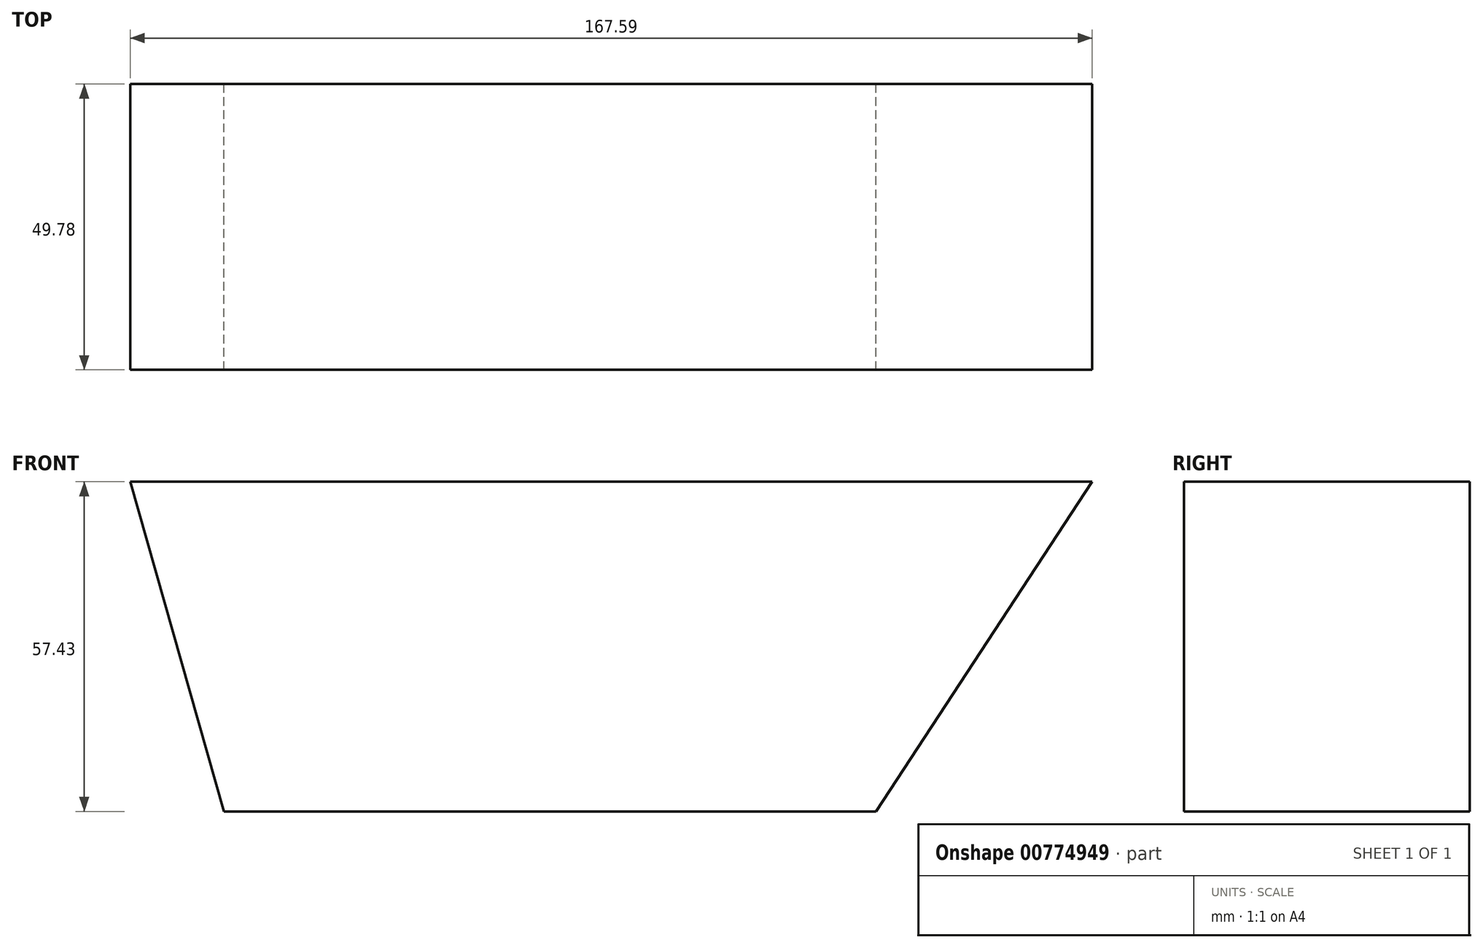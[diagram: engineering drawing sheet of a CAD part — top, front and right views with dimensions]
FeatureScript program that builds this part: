
annotation { "Feature Type Name" : "Feature", "Feature Type Description" : "" }
export const myFeature = defineFeature(function(context is Context, id is Id, definition is map)
    precondition{}
    {
        {
            var Q0;
            Q0=qCreatedBy(makeId("Front.planeOp"),FACE);
            var sketch = newSketch(context, id + "F0", { "sketchPlane" : qUnion([Q0])});
            skLineSegment(sketch, "E0", {"start": v(-110.16, 45.1) * mm, "end": v(-93.84, -12.34) * mm});
            skLineSegment(sketch, "E1", {"start": v(-110.16, 45.1) * mm, "end": v(57.43, 45.1) * mm});
            skLineSegment(sketch, "E2", {"start": v(-93.84, -12.34) * mm, "end": v(19.77, -12.34) * mm});
            skLineSegment(sketch, "E3", {"start": v(19.77, -12.34) * mm, "end": v(57.43, 45.1) * mm});
            skSolve(sketch);
        }
        {
            var Q0;
            Q0=makeQuery(id+"F0.imprint","IMPRINT",FACE,{"disambiguationData":[TD([[makeQuery(id+"F0.imprint","IMPRINT",EDGE,{"derivedFrom":sQuery(id+"F0.wireOp",EDGE,"E0")}),1.0]])]});
            extrude(context, id + "F1", {"entities" : qUnion([Q0]), "depth" : 49.78 * mm, "offsetDistance" : 25.4 * mm});
        }
    });
